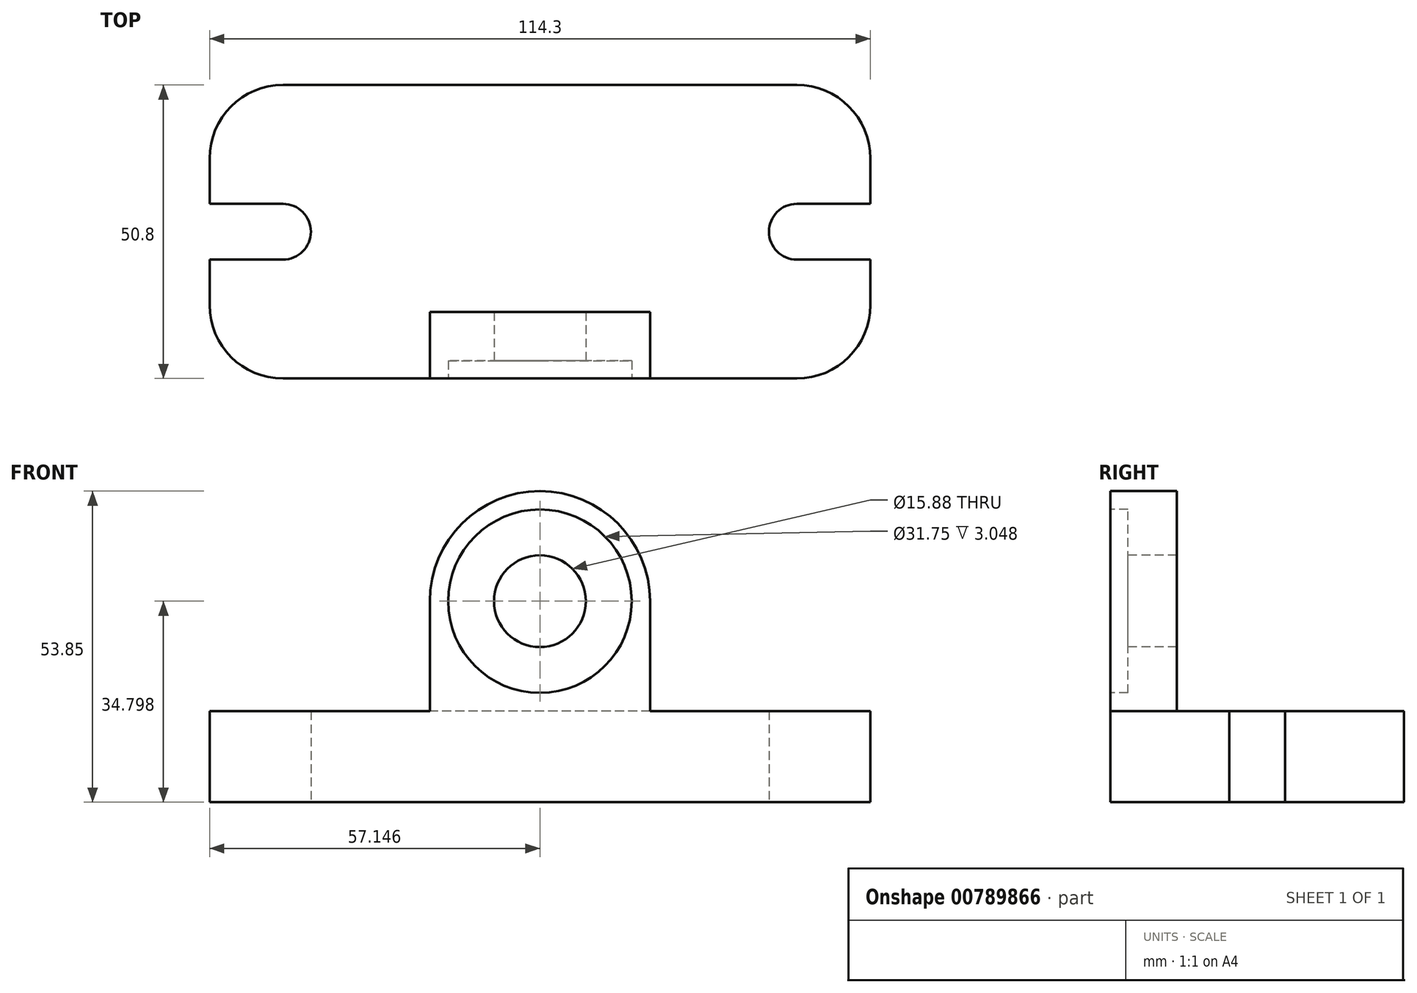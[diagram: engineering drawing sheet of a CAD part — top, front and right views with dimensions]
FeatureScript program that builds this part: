
annotation { "Feature Type Name" : "Feature", "Feature Type Description" : "" }
export const myFeature = defineFeature(function(context is Context, id is Id, definition is map)
    precondition{}
    {
        {
            var Q0;
            Q0=qCreatedBy(makeId("Top.planeOp"),FACE);
            var sketch = newSketch(context, id + "F0", { "sketchPlane" : qUnion([Q0])});
            skLineSegment(sketch, "E0.bottom", {"start": v(58.13, 0) * mm, "end": v(-30.77, 0) * mm});
            skLineSegment(sketch, "E0.top", {"start": v(58.13, 50.8) * mm, "end": v(-30.77, 50.8) * mm});
            skLineSegment(sketch, "E0.left", {"start": v(70.83, 12.7) * mm, "end": v(70.83, 20.57) * mm});
            skLineSegment(sketch, "E0.right", {"start": v(-43.47, 12.7) * mm, "end": v(-43.47, 20.57) * mm});
            skLineSegment(sketch, "E1", {"start": v(-43.47, 25.4) * mm, "end": v(-27.17, 25.4) * mm, "construction": true});
            skLineSegment(sketch, "E2", {"start": v(-43.47, 20.57) * mm, "end": v(-30.77, 20.57) * mm});
            skLineSegment(sketch, "E3", {"start": v(-43.47, 30.23) * mm, "end": v(-30.77, 30.23) * mm});
            skArc(sketch, "E4", {"start": v(-30.77, 20.57) * mm, "mid": v(-25.95, 25.4) * mm, "end": v(-30.77, 30.23) * mm});
            skLineSegment(sketch, "E5.trimOffspring", {"start": v(-43.47, 30.23) * mm, "end": v(-43.47, 38.1) * mm});
            skLineSegment(sketch, "E6", {"start": v(70.83, 25.4) * mm, "end": v(53.6, 25.4) * mm, "construction": true});
            skLineSegment(sketch, "E7", {"start": v(70.83, 20.57) * mm, "end": v(58.13, 20.57) * mm});
            skLineSegment(sketch, "E8", {"start": v(70.83, 30.23) * mm, "end": v(58.13, 30.23) * mm});
            skArc(sketch, "E9", {"start": v(58.13, 30.23) * mm, "mid": v(53.3, 25.4) * mm, "end": v(58.13, 20.57) * mm});
            skLineSegment(sketch, "E10.trimOffspring", {"start": v(70.83, 30.23) * mm, "end": v(70.83, 38.1) * mm});
            skPoint(sketch, "E11.visualSharp", {"position": v(-43.47, 50.8) * mm});
            skArc(sketch, "E11.filletArc", {"start": v(-30.77, 50.8) * mm, "mid": v(-39.75, 47.08) * mm, "end": v(-43.47, 38.1) * mm});
            skPoint(sketch, "E12.visualSharp", {"position": v(-43.47, 0) * mm});
            skArc(sketch, "E12.filletArc", {"start": v(-43.47, 12.7) * mm, "mid": v(-39.75, 3.72) * mm, "end": v(-30.77, 0) * mm});
            skPoint(sketch, "E13.visualSharp", {"position": v(70.83, 0) * mm});
            skArc(sketch, "E13.filletArc", {"start": v(58.13, 0) * mm, "mid": v(67.1, 3.72) * mm, "end": v(70.83, 12.7) * mm});
            skPoint(sketch, "E14.visualSharp", {"position": v(70.83, 50.8) * mm});
            skArc(sketch, "E14.filletArc", {"start": v(70.83, 38.1) * mm, "mid": v(67.1, 47.08) * mm, "end": v(58.13, 50.8) * mm});
            skSolve(sketch);
        }
        {
            var Q0;
            Q0=makeQuery(id+"F0.imprint","IMPRINT",FACE,{"disambiguationData":[TD([[makeQuery(id+"F0.imprint","IMPRINT",EDGE,{"derivedFrom":sQuery(id+"F0.wireOp",EDGE,"E0.bottom")}),-1.0]])]});
            extrude(context, id + "F1", {"entities" : qUnion([Q0]), "depth" : 15.75 * mm, "offsetDistance" : 25.4 * mm});
        }
        {
            var Q0;
            Q0=makeQuery(id+"F1.opExtrude","CAP_FACE",FACE,{"disambiguationData":[OSD([sQuery(id+"F0.wireOp",EDGE,"E0.bottom"),sQuery(id+"F0.wireOp",EDGE,"E0.top"),sQuery(id+"F0.wireOp",EDGE,"E0.left"),sQuery(id+"F0.wireOp",EDGE,"E0.right"),sQuery(id+"F0.wireOp",EDGE,"E2"),sQuery(id+"F0.wireOp",EDGE,"E3"),sQuery(id+"F0.wireOp",EDGE,"E4"),sQuery(id+"F0.wireOp",EDGE,"E5.trimOffspring"),sQuery(id+"F0.wireOp",EDGE,"E7"),sQuery(id+"F0.wireOp",EDGE,"E8"),sQuery(id+"F0.wireOp",EDGE,"E9"),sQuery(id+"F0.wireOp",EDGE,"E10.trimOffspring"),sQuery(id+"F0.wireOp",EDGE,"E11.filletArc"),sQuery(id+"F0.wireOp",EDGE,"E12.filletArc"),sQuery(id+"F0.wireOp",EDGE,"E13.filletArc"),sQuery(id+"F0.wireOp",EDGE,"E14.filletArc")])],"isStart":false});
            var sketch = newSketch(context, id + "F2", { "sketchPlane" : qUnion([Q0])});
            skLineSegment(sketch, "E15.bottom", {"start": v(32.73, 0) * mm, "end": v(-5.37, 0) * mm});
            skLineSegment(sketch, "E15.top", {"start": v(32.73, 11.5) * mm, "end": v(-5.37, 11.5) * mm});
            skLineSegment(sketch, "E15.left", {"start": v(32.73, 0) * mm, "end": v(32.73, 11.5) * mm});
            skLineSegment(sketch, "E15.right", {"start": v(-5.37, 0) * mm, "end": v(-5.37, 11.5) * mm});
            skSolve(sketch);
        }
        {
            var Q0;
            Q0=makeQuery(id+"F2.imprint","IMPRINT",FACE,{"disambiguationData":[TD([[makeQuery(id+"F2.imprint","IMPRINT",EDGE,{"derivedFrom":sQuery(id+"F2.wireOp",EDGE,"E15.bottom")}),-1.0]])]});
            extrude(context, id + "F3", {"entities" : qUnion([Q0]), "operationType" : NewBodyOperationType.ADD, "depth" : 38.1 * mm, "offsetDistance" : 25.4 * mm});
        }
        {
            var Q0;
            Q0=makeQuery(id+"F3.opExtrude","CAP_EDGE",EDGE,{"disambiguationData":[OSD([sQuery(id+"F2.wireOp",EDGE,"E15.right")])],"isStart":false});
            var Q1;
            Q1=makeQuery(id+"F3.opExtrude","CAP_EDGE",EDGE,{"disambiguationData":[OSD([sQuery(id+"F2.wireOp",EDGE,"E15.left")])],"isStart":false});
            fillet(context, id + "F4", {"entities" : qUnion([Q0, Q1]), "radius" : 19.05 * mm, "tangentPropagation" : true, "allowEdgeOverflow" : false});
        }
        {
            var Q0;
            Q0=makeQuery(id+"F3.boolean.opBoolean","MERGE",FACE,{"derivedFrom":[makeQuery(id+"F1.opExtrude","SWEPT_FACE",FACE,{"disambiguationData":[OSD([sQuery(id+"F0.wireOp",EDGE,"E0.bottom")])]}),makeQuery(id+"F3.opExtrude","SWEPT_FACE",FACE,{"disambiguationData":[OSD([sQuery(id+"F2.wireOp",EDGE,"E15.bottom")])]})]});
            var sketch = newSketch(context, id + "F5", { "sketchPlane" : qUnion([Q0])});
            skCircle(sketch, "E16", {"center": v(13.68, 34.8) * mm, "radius": 15.88 * mm});
            skCircle(sketch, "E17", {"center": v(13.68, 34.8) * mm, "radius": 5.86 * mm});
            skSolve(sketch);
        }
        {
            var Q0;
            Q0=sQuery(id+"F5.wireOp",VERTEX,"E16.center");
            var Q1;
            Q1=makeQuery(id+"F1.opExtrude","SWEPT_BODY",BODY,{"disambiguationData":[OSD([sQuery(id+"F0.wireOp",EDGE,"E0.bottom"),sQuery(id+"F0.wireOp",EDGE,"E0.top"),sQuery(id+"F0.wireOp",EDGE,"E0.left"),sQuery(id+"F0.wireOp",EDGE,"E0.right"),sQuery(id+"F0.wireOp",EDGE,"E2"),sQuery(id+"F0.wireOp",EDGE,"E3"),sQuery(id+"F0.wireOp",EDGE,"E4"),sQuery(id+"F0.wireOp",EDGE,"E5.trimOffspring"),sQuery(id+"F0.wireOp",EDGE,"E7"),sQuery(id+"F0.wireOp",EDGE,"E8"),sQuery(id+"F0.wireOp",EDGE,"E9"),sQuery(id+"F0.wireOp",EDGE,"E10.trimOffspring"),sQuery(id+"F0.wireOp",EDGE,"E11.filletArc"),sQuery(id+"F0.wireOp",EDGE,"E12.filletArc"),sQuery(id+"F0.wireOp",EDGE,"E13.filletArc"),sQuery(id+"F0.wireOp",EDGE,"E14.filletArc")])]});
            hole(context, id + "F6", {"style" : HoleStyle.SIMPLE, "endStyle" : HoleEndStyle.THROUGH, "holeDiameter" : 15.88 * mm, "majorDiameter" : 6.35 * mm, "isTappedThrough" : true, "tappedDepth" : 12.7 * mm, "tapClearance" : 3, "locations" : qUnion([Q0]), "scope" : qUnion([Q1])});
        }
        {
            var Q0;
            Q0=makeQuery(id+"F3.boolean.opBoolean","MERGE",FACE,{"derivedFrom":[makeQuery(id+"F1.opExtrude","SWEPT_FACE",FACE,{"disambiguationData":[OSD([sQuery(id+"F0.wireOp",EDGE,"E0.bottom")])]}),makeQuery(id+"F3.opExtrude","SWEPT_FACE",FACE,{"disambiguationData":[OSD([sQuery(id+"F2.wireOp",EDGE,"E15.bottom")])]})]});
            var sketch = newSketch(context, id + "F7", { "sketchPlane" : qUnion([Q0])});
            skCircle(sketch, "E18", {"center": v(13.68, 34.8) * mm, "radius": 15.87 * mm});
            skSolve(sketch);
        }
        {
            var Q0;
            Q0=makeQuery(id+"F7.imprint","IMPRINT",FACE,{"disambiguationData":[TD([[makeQuery(id+"F7.imprint","IMPRINT",EDGE,{"derivedFrom":sQuery(id+"F7.wireOp",EDGE,"E18")}),1.0]])]});
            extrude(context, id + "F8", {"entities" : qUnion([Q0]), "operationType" : NewBodyOperationType.REMOVE, "oppositeDirection" : true, "depth" : 3.05 * mm, "offsetDistance" : 25.4 * mm});
        }
    });
